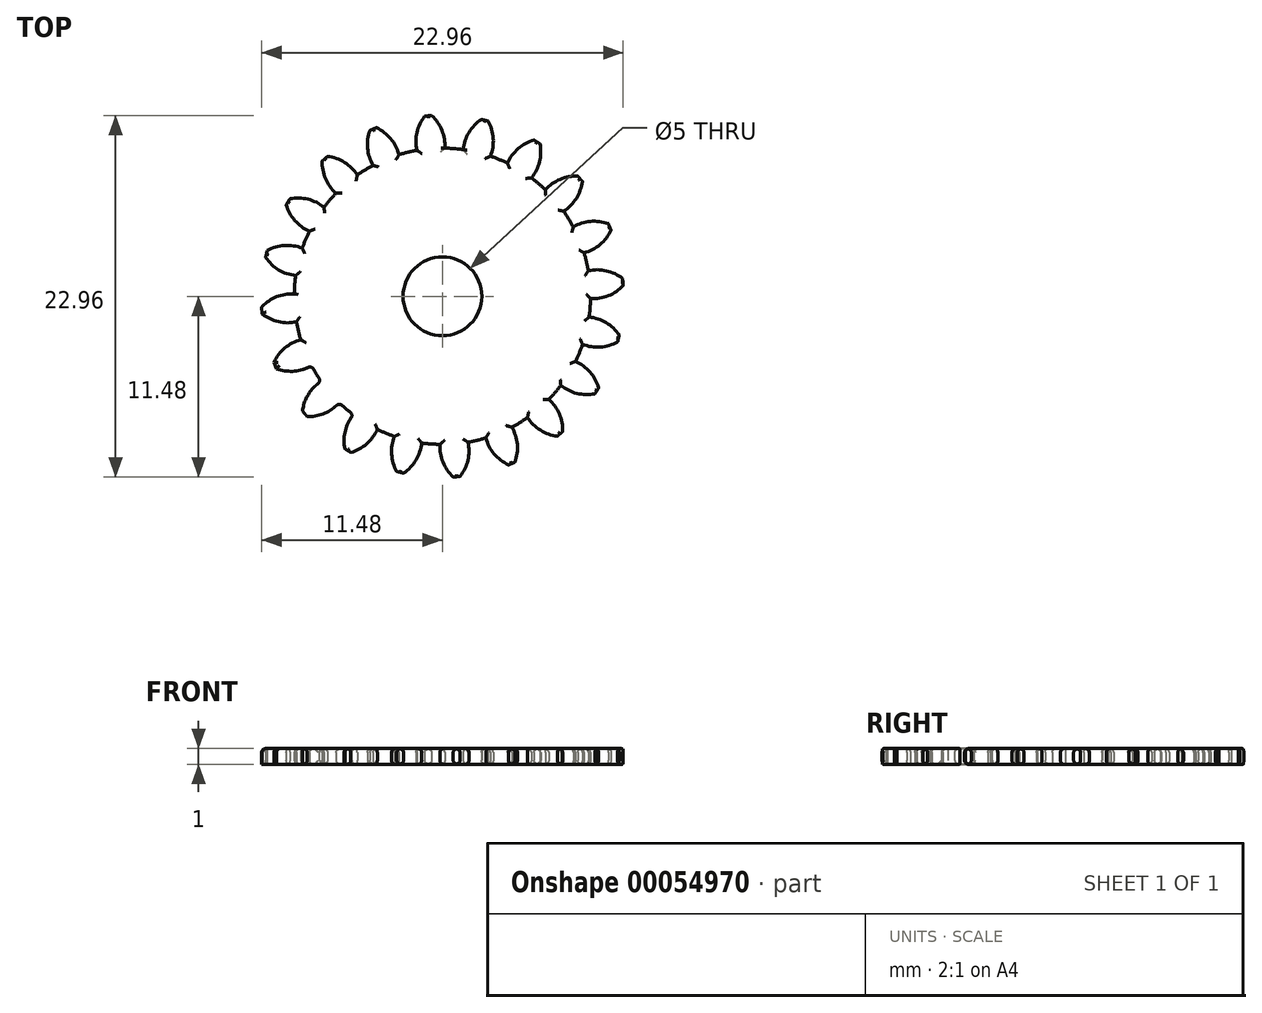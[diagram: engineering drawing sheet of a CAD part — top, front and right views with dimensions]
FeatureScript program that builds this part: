
annotation { "Feature Type Name" : "Feature", "Feature Type Description" : "" }
export const myFeature = defineFeature(function(context is Context, id is Id, definition is map)
    precondition{}
    {
        {
            assignVariable(context, id + "F0", {"name" : "GearDepth", "anyValue" : 1});
        }
        {
            assignVariable(context, id + "F1", {"name" : "TeethFillet", "anyValue" : getVariable(context, 'GearDepth') * .25});
        }
        {
            var Q0;
            Q0=qCreatedBy(makeId("Top.planeOp"),FACE);
            var sketch = newSketch(context, id + "F2", { "sketchPlane" : qUnion([Q0])});
            skCircle(sketch, "E0", {"center": v(0, 0) * mm, "radius": 9.4 * mm});
            skCircle(sketch, "E1", {"center": v(0, 0) * mm, "radius": 10.45 * mm, "construction": true});
            skCircle(sketch, "E2", {"center": v(0, 0) * mm, "radius": 11.5 * mm, "construction": true});
            skLineSegment(sketch, "E3", {"start": v(0, 0) * mm, "end": v(0, 17.6) * mm, "construction": true});
            skLineSegment(sketch, "E4", {"start": v(0, 0) * mm, "end": v(-1.42, 18) * mm, "construction": true});
            skLineSegment(sketch, "E5", {"start": v(0, 10.45) * mm, "end": v(-10.54, 10.45) * mm, "construction": true});
            skLineSegment(sketch, "E6", {"start": v(0, 10.45) * mm, "end": v(-10.3, 6.7) * mm, "construction": true});
            skCircle(sketch, "E7", {"center": v(0, 10.45) * mm, "radius": 2.61 * mm, "construction": true});
            skCircle(sketch, "E8", {"center": v(-2.46, 9.56) * mm, "radius": 2.61 * mm, "construction": true});
            skArc(sketch, "E9", {"start": v(-4.91, 10.45) * mm, "mid": v(-4.92, 10.42) * mm, "end": v(-4.94, 10.39) * mm});
            skArc(sketch, "E10.trimOffspring", {"start": v(0.15, 9.4) * mm, "mid": v(-0.03, 10.54) * mm, "end": v(-0.68, 11.48) * mm});
            skArc(sketch, "E11.MirrorCS", {"start": v(-1.62, 9.27) * mm, "mid": v(-1.62, 10.41) * mm, "end": v(-1.12, 11.45) * mm});
            skLineSegment(sketch, "E12", {"start": v(-1.12, 11.45) * mm, "end": v(-0.68, 11.48) * mm});
            skArc(sketch, "E13.1.0", {"start": v(-2.76, 9) * mm, "mid": v(-3.29, 10.01) * mm, "end": v(-4.2, 10.7) * mm});
            skLineSegment(sketch, "E13.1.1", {"start": v(-4.6, 10.54) * mm, "end": v(-4.2, 10.7) * mm});
            skArc(sketch, "E13.1.2", {"start": v(-4.4, 8.31) * mm, "mid": v(-4.76, 9.4) * mm, "end": v(-4.6, 10.54) * mm});
            skArc(sketch, "E13.2.0", {"start": v(-5.4, 7.7) * mm, "mid": v(-6.22, 8.5) * mm, "end": v(-7.3, 8.89) * mm});
            skLineSegment(sketch, "E13.2.1", {"start": v(-7.64, 8.6) * mm, "end": v(-7.3, 8.89) * mm});
            skArc(sketch, "E13.2.2", {"start": v(-6.76, 6.54) * mm, "mid": v(-7.43, 7.47) * mm, "end": v(-7.64, 8.6) * mm});
            skArc(sketch, "E13.3.0", {"start": v(-7.52, 5.65) * mm, "mid": v(-8.54, 6.17) * mm, "end": v(-9.69, 6.2) * mm});
            skLineSegment(sketch, "E13.3.1", {"start": v(-9.92, 5.82) * mm, "end": v(-9.69, 6.2) * mm});
            skArc(sketch, "E13.3.2", {"start": v(-8.45, 4.13) * mm, "mid": v(-9.37, 4.81) * mm, "end": v(-9.92, 5.82) * mm});
            skArc(sketch, "E13.4.0", {"start": v(-8.9, 3.05) * mm, "mid": v(-10.03, 3.23) * mm, "end": v(-11.13, 2.9) * mm});
            skLineSegment(sketch, "E13.4.1", {"start": v(-11.23, 2.47) * mm, "end": v(-11.13, 2.9) * mm});
            skArc(sketch, "E13.4.2", {"start": v(-9.32, 1.32) * mm, "mid": v(-10.4, 1.68) * mm, "end": v(-11.23, 2.47) * mm});
            skArc(sketch, "E13.5.0", {"start": v(-9.4, 0.15) * mm, "mid": v(-10.54, -0.03) * mm, "end": v(-11.48, -0.68) * mm});
            skLineSegment(sketch, "E13.5.1", {"start": v(-11.45, -1.12) * mm, "end": v(-11.48, -0.68) * mm});
            skArc(sketch, "E13.5.2", {"start": v(-9.27, -1.62) * mm, "mid": v(-10.41, -1.62) * mm, "end": v(-11.45, -1.12) * mm});
            skArc(sketch, "E13.6.0", {"start": v(-9, -2.76) * mm, "mid": v(-10.01, -3.29) * mm, "end": v(-10.7, -4.2) * mm});
            skLineSegment(sketch, "E13.6.1", {"start": v(-10.54, -4.6) * mm, "end": v(-10.7, -4.2) * mm});
            skArc(sketch, "E13.6.2", {"start": v(-8.31, -4.4) * mm, "mid": v(-9.4, -4.76) * mm, "end": v(-10.54, -4.6) * mm});
            skArc(sketch, "E13.7.0", {"start": v(-7.7, -5.4) * mm, "mid": v(-8.5, -6.22) * mm, "end": v(-8.89, -7.3) * mm});
            skLineSegment(sketch, "E13.7.1", {"start": v(-8.6, -7.64) * mm, "end": v(-8.89, -7.3) * mm});
            skArc(sketch, "E13.7.2", {"start": v(-6.54, -6.76) * mm, "mid": v(-7.47, -7.43) * mm, "end": v(-8.6, -7.64) * mm});
            skArc(sketch, "E13.8.0", {"start": v(-5.65, -7.52) * mm, "mid": v(-6.17, -8.54) * mm, "end": v(-6.2, -9.69) * mm});
            skLineSegment(sketch, "E13.8.1", {"start": v(-5.82, -9.92) * mm, "end": v(-6.2, -9.69) * mm});
            skArc(sketch, "E13.8.2", {"start": v(-4.13, -8.45) * mm, "mid": v(-4.81, -9.37) * mm, "end": v(-5.82, -9.92) * mm});
            skArc(sketch, "E13.9.0", {"start": v(-3.05, -8.9) * mm, "mid": v(-3.23, -10.03) * mm, "end": v(-2.9, -11.13) * mm});
            skLineSegment(sketch, "E13.9.1", {"start": v(-2.47, -11.23) * mm, "end": v(-2.9, -11.13) * mm});
            skArc(sketch, "E13.9.2", {"start": v(-1.32, -9.32) * mm, "mid": v(-1.68, -10.4) * mm, "end": v(-2.47, -11.23) * mm});
            skArc(sketch, "E13.10.0", {"start": v(-0.15, -9.4) * mm, "mid": v(0.03, -10.54) * mm, "end": v(0.68, -11.48) * mm});
            skLineSegment(sketch, "E13.10.1", {"start": v(1.12, -11.45) * mm, "end": v(0.68, -11.48) * mm});
            skArc(sketch, "E13.10.2", {"start": v(1.62, -9.27) * mm, "mid": v(1.62, -10.41) * mm, "end": v(1.12, -11.45) * mm});
            skArc(sketch, "E13.11.0", {"start": v(2.76, -9) * mm, "mid": v(3.29, -10.01) * mm, "end": v(4.2, -10.7) * mm});
            skLineSegment(sketch, "E13.11.1", {"start": v(4.6, -10.54) * mm, "end": v(4.2, -10.7) * mm});
            skArc(sketch, "E13.11.2", {"start": v(4.4, -8.31) * mm, "mid": v(4.76, -9.4) * mm, "end": v(4.6, -10.54) * mm});
            skArc(sketch, "E13.12.0", {"start": v(5.4, -7.7) * mm, "mid": v(6.22, -8.5) * mm, "end": v(7.3, -8.89) * mm});
            skLineSegment(sketch, "E13.12.1", {"start": v(7.64, -8.6) * mm, "end": v(7.3, -8.89) * mm});
            skArc(sketch, "E13.12.2", {"start": v(6.76, -6.54) * mm, "mid": v(7.43, -7.47) * mm, "end": v(7.64, -8.6) * mm});
            skArc(sketch, "E13.13.0", {"start": v(7.52, -5.65) * mm, "mid": v(8.54, -6.17) * mm, "end": v(9.69, -6.2) * mm});
            skLineSegment(sketch, "E13.13.1", {"start": v(9.92, -5.82) * mm, "end": v(9.69, -6.2) * mm});
            skArc(sketch, "E13.13.2", {"start": v(8.45, -4.13) * mm, "mid": v(9.37, -4.81) * mm, "end": v(9.92, -5.82) * mm});
            skArc(sketch, "E13.14.0", {"start": v(8.9, -3.05) * mm, "mid": v(10.03, -3.23) * mm, "end": v(11.13, -2.9) * mm});
            skLineSegment(sketch, "E13.14.1", {"start": v(11.23, -2.47) * mm, "end": v(11.13, -2.9) * mm});
            skArc(sketch, "E13.14.2", {"start": v(9.32, -1.32) * mm, "mid": v(10.4, -1.68) * mm, "end": v(11.23, -2.47) * mm});
            skArc(sketch, "E13.15.0", {"start": v(9.4, -0.15) * mm, "mid": v(10.54, 0.03) * mm, "end": v(11.48, 0.68) * mm});
            skLineSegment(sketch, "E13.15.1", {"start": v(11.45, 1.12) * mm, "end": v(11.48, 0.68) * mm});
            skArc(sketch, "E13.15.2", {"start": v(9.27, 1.62) * mm, "mid": v(10.41, 1.62) * mm, "end": v(11.45, 1.12) * mm});
            skArc(sketch, "E13.16.0", {"start": v(9, 2.76) * mm, "mid": v(10.01, 3.29) * mm, "end": v(10.7, 4.2) * mm});
            skLineSegment(sketch, "E13.16.1", {"start": v(10.54, 4.6) * mm, "end": v(10.7, 4.2) * mm});
            skArc(sketch, "E13.16.2", {"start": v(8.31, 4.4) * mm, "mid": v(9.4, 4.76) * mm, "end": v(10.54, 4.6) * mm});
            skArc(sketch, "E13.17.0", {"start": v(7.7, 5.4) * mm, "mid": v(8.5, 6.22) * mm, "end": v(8.89, 7.3) * mm});
            skLineSegment(sketch, "E13.17.1", {"start": v(8.6, 7.64) * mm, "end": v(8.89, 7.3) * mm});
            skArc(sketch, "E13.17.2", {"start": v(6.54, 6.76) * mm, "mid": v(7.47, 7.43) * mm, "end": v(8.6, 7.64) * mm});
            skArc(sketch, "E13.18.0", {"start": v(5.65, 7.52) * mm, "mid": v(6.17, 8.54) * mm, "end": v(6.2, 9.69) * mm});
            skLineSegment(sketch, "E13.18.1", {"start": v(5.82, 9.92) * mm, "end": v(6.2, 9.69) * mm});
            skArc(sketch, "E13.18.2", {"start": v(4.13, 8.45) * mm, "mid": v(4.81, 9.37) * mm, "end": v(5.82, 9.92) * mm});
            skArc(sketch, "E13.19.0", {"start": v(3.05, 8.9) * mm, "mid": v(3.23, 10.03) * mm, "end": v(2.9, 11.13) * mm});
            skLineSegment(sketch, "E13.19.1", {"start": v(2.47, 11.23) * mm, "end": v(2.9, 11.13) * mm});
            skArc(sketch, "E13.19.2", {"start": v(1.32, 9.32) * mm, "mid": v(1.68, 10.4) * mm, "end": v(2.47, 11.23) * mm});
            skCircle(sketch, "E14", {"center": v(0, 0) * mm, "radius": 2.5 * mm});
            skSolve(sketch);
        }
        {
            var Q0;
            {var subQ0=sQuery(id+"F2.wireOp",EDGE,"E10.trimOffspring");Q0=makeQuery(id+"F2.imprint","IMPRINT",FACE,{"disambiguationData":[TD([[makeQuery(id+"F2.imprint","IMPRINT",EDGE,{"derivedFrom":subQ0}),1.0]])]});}
            var Q1;
            {var subQ0=sQuery(id+"F2.wireOp",EDGE,"E0");var subQ1=makeQuery(id+"F2.imprint","INTERSECT",VERTEX,{"derivedFrom":[subQ0,sQuery(id+"F2.wireOp",EDGE,"E10.trimOffspring")]});Q1=makeQuery(id+"F2.imprint","IMPRINT",FACE,{"disambiguationData":[TD([[makeQuery(id+"F2.imprint","IMPRINT",EDGE,{"disambiguationData":[TD([[subQ1,-1.0]])],"derivedFrom":subQ0}),1.0]])]});}
            var Q2;
            {var subQ0=sQuery(id+"F2.wireOp",EDGE,"E13.1.0");Q2=makeQuery(id+"F2.imprint","IMPRINT",FACE,{"disambiguationData":[TD([[makeQuery(id+"F2.imprint","IMPRINT",EDGE,{"derivedFrom":subQ0}),1.0]])]});}
            var Q3;
            {var subQ0=sQuery(id+"F2.wireOp",EDGE,"E13.2.0");Q3=makeQuery(id+"F2.imprint","IMPRINT",FACE,{"disambiguationData":[TD([[makeQuery(id+"F2.imprint","IMPRINT",EDGE,{"derivedFrom":subQ0}),1.0]])]});}
            var Q4;
            {var subQ0=sQuery(id+"F2.wireOp",EDGE,"E13.3.0");Q4=makeQuery(id+"F2.imprint","IMPRINT",FACE,{"disambiguationData":[TD([[makeQuery(id+"F2.imprint","IMPRINT",EDGE,{"derivedFrom":subQ0}),1.0]])]});}
            var Q5;
            {var subQ0=sQuery(id+"F2.wireOp",EDGE,"E13.4.0");Q5=makeQuery(id+"F2.imprint","IMPRINT",FACE,{"disambiguationData":[TD([[makeQuery(id+"F2.imprint","IMPRINT",EDGE,{"derivedFrom":subQ0}),1.0]])]});}
            var Q6;
            {var subQ0=sQuery(id+"F2.wireOp",EDGE,"E13.5.0");Q6=makeQuery(id+"F2.imprint","IMPRINT",FACE,{"disambiguationData":[TD([[makeQuery(id+"F2.imprint","IMPRINT",EDGE,{"derivedFrom":subQ0}),1.0]])]});}
            var Q7;
            {var subQ0=sQuery(id+"F2.wireOp",EDGE,"E13.6.0");Q7=makeQuery(id+"F2.imprint","IMPRINT",FACE,{"disambiguationData":[TD([[makeQuery(id+"F2.imprint","IMPRINT",EDGE,{"derivedFrom":subQ0}),1.0]])]});}
            var Q8;
            {var subQ0=sQuery(id+"F2.wireOp",EDGE,"E13.7.0");Q8=makeQuery(id+"F2.imprint","IMPRINT",FACE,{"disambiguationData":[TD([[makeQuery(id+"F2.imprint","IMPRINT",EDGE,{"derivedFrom":subQ0}),1.0]])]});}
            var Q9;
            {var subQ0=sQuery(id+"F2.wireOp",EDGE,"E13.8.0");Q9=makeQuery(id+"F2.imprint","IMPRINT",FACE,{"disambiguationData":[TD([[makeQuery(id+"F2.imprint","IMPRINT",EDGE,{"derivedFrom":subQ0}),1.0]])]});}
            var Q10;
            {var subQ0=sQuery(id+"F2.wireOp",EDGE,"E13.9.0");Q10=makeQuery(id+"F2.imprint","IMPRINT",FACE,{"disambiguationData":[TD([[makeQuery(id+"F2.imprint","IMPRINT",EDGE,{"derivedFrom":subQ0}),1.0]])]});}
            var Q11;
            {var subQ0=sQuery(id+"F2.wireOp",EDGE,"E13.10.0");Q11=makeQuery(id+"F2.imprint","IMPRINT",FACE,{"disambiguationData":[TD([[makeQuery(id+"F2.imprint","IMPRINT",EDGE,{"derivedFrom":subQ0}),1.0]])]});}
            var Q12;
            {var subQ0=sQuery(id+"F2.wireOp",EDGE,"E13.11.0");Q12=makeQuery(id+"F2.imprint","IMPRINT",FACE,{"disambiguationData":[TD([[makeQuery(id+"F2.imprint","IMPRINT",EDGE,{"derivedFrom":subQ0}),1.0]])]});}
            var Q13;
            {var subQ0=sQuery(id+"F2.wireOp",EDGE,"E13.12.0");Q13=makeQuery(id+"F2.imprint","IMPRINT",FACE,{"disambiguationData":[TD([[makeQuery(id+"F2.imprint","IMPRINT",EDGE,{"derivedFrom":subQ0}),1.0]])]});}
            var Q14;
            {var subQ0=sQuery(id+"F2.wireOp",EDGE,"E13.13.0");Q14=makeQuery(id+"F2.imprint","IMPRINT",FACE,{"disambiguationData":[TD([[makeQuery(id+"F2.imprint","IMPRINT",EDGE,{"derivedFrom":subQ0}),1.0]])]});}
            var Q15;
            {var subQ0=sQuery(id+"F2.wireOp",EDGE,"E13.14.0");Q15=makeQuery(id+"F2.imprint","IMPRINT",FACE,{"disambiguationData":[TD([[makeQuery(id+"F2.imprint","IMPRINT",EDGE,{"derivedFrom":subQ0}),1.0]])]});}
            var Q16;
            {var subQ0=sQuery(id+"F2.wireOp",EDGE,"E13.15.0");Q16=makeQuery(id+"F2.imprint","IMPRINT",FACE,{"disambiguationData":[TD([[makeQuery(id+"F2.imprint","IMPRINT",EDGE,{"derivedFrom":subQ0}),1.0]])]});}
            var Q17;
            {var subQ0=sQuery(id+"F2.wireOp",EDGE,"E13.16.0");Q17=makeQuery(id+"F2.imprint","IMPRINT",FACE,{"disambiguationData":[TD([[makeQuery(id+"F2.imprint","IMPRINT",EDGE,{"derivedFrom":subQ0}),1.0]])]});}
            var Q18;
            {var subQ0=sQuery(id+"F2.wireOp",EDGE,"E13.17.0");Q18=makeQuery(id+"F2.imprint","IMPRINT",FACE,{"disambiguationData":[TD([[makeQuery(id+"F2.imprint","IMPRINT",EDGE,{"derivedFrom":subQ0}),1.0]])]});}
            var Q19;
            {var subQ0=sQuery(id+"F2.wireOp",EDGE,"E13.18.0");Q19=makeQuery(id+"F2.imprint","IMPRINT",FACE,{"disambiguationData":[TD([[makeQuery(id+"F2.imprint","IMPRINT",EDGE,{"derivedFrom":subQ0}),1.0]])]});}
            var Q20;
            {var subQ0=sQuery(id+"F2.wireOp",EDGE,"E13.19.0");Q20=makeQuery(id+"F2.imprint","IMPRINT",FACE,{"disambiguationData":[TD([[makeQuery(id+"F2.imprint","IMPRINT",EDGE,{"derivedFrom":subQ0}),1.0]])]});}
            var Q21;
            Q21=sQuery(id+"F2.wireOp",EDGE,"E0");
            var Q22;
            Q22=sQuery(id+"F2.wireOp",EDGE,"E10.trimOffspring");
            var Q23;
            Q23=sQuery(id+"F2.wireOp",EDGE,"E12");
            var Q24;
            Q24=sQuery(id+"F2.wireOp",EDGE,"E11.MirrorCS");
            extrude(context, id + "F3", {"entities" : qUnion([Q0, Q1, Q2, Q3, Q4, Q5, Q6, Q7, Q8, Q9, Q10, Q11, Q12, Q13, Q14, Q15, Q16, Q17, Q18, Q19, Q20]), "surfaceEntities" : qUnion([Q21, Q22, Q23, Q24]), "depth" : (getVariable(context, 'GearDepth')) * mm});
        }
        {
            var Q0;
            Q0=makeQuery(id+"F3.opExtrude","CAP_EDGE",EDGE,{"disambiguationData":[OSD([sQuery(id+"F2.wireOp",EDGE,"E13.5.2")])],"isStart":false});
            var Q1;
            Q1=makeQuery(id+"F3.opExtrude","CAP_EDGE",EDGE,{"disambiguationData":[OSD([sQuery(id+"F2.wireOp",EDGE,"E13.5.1")])],"isStart":false});
            var Q2;
            {var subQ0=sQuery(id+"F2.wireOp",EDGE,"E0");Q2=makeQuery(id+"F3.opExtrude","CAP_EDGE",EDGE,{"disambiguationData":[OSD([subQ0]),TDD([makeQuery(id+"F2.imprint","IMPRINT",EDGE,{"disambiguationData":[TD([[makeQuery(id+"F2.imprint","INTERSECT",VERTEX,{"derivedFrom":[subQ0,sQuery(id+"F2.wireOp",EDGE,"E13.5.2")]}),-1.0]])],"derivedFrom":subQ0})])],"isStart":false});}
            var Q3;
            Q3=makeQuery(id+"F3.opExtrude","CAP_EDGE",EDGE,{"disambiguationData":[OSD([sQuery(id+"F2.wireOp",EDGE,"E13.6.0")])],"isStart":false});
            var Q4;
            Q4=makeQuery(id+"F3.opExtrude","CAP_EDGE",EDGE,{"disambiguationData":[OSD([sQuery(id+"F2.wireOp",EDGE,"E13.6.1")])],"isStart":false});
            var Q5;
            Q5=makeQuery(id+"F3.opExtrude","CAP_EDGE",EDGE,{"disambiguationData":[OSD([sQuery(id+"F2.wireOp",EDGE,"E13.6.2")])],"isStart":false});
            var Q6;
            {var subQ0=sQuery(id+"F2.wireOp",EDGE,"E0");Q6=makeQuery(id+"F3.opExtrude","SWEPT_FACE",FACE,{"disambiguationData":[OSD([subQ0]),TDD([makeQuery(id+"F2.imprint","IMPRINT",EDGE,{"disambiguationData":[TD([[makeQuery(id+"F2.imprint","INTERSECT",VERTEX,{"derivedFrom":[subQ0,sQuery(id+"F2.wireOp",EDGE,"E13.6.2")]}),-1.0]])],"derivedFrom":subQ0})])]});}
            var Q7;
            {var subQ0=sQuery(id+"F2.wireOp",EDGE,"E0");Q7=makeQuery(id+"F3.opExtrude","CAP_EDGE",EDGE,{"disambiguationData":[OSD([subQ0]),TDD([makeQuery(id+"F2.imprint","IMPRINT",EDGE,{"disambiguationData":[TD([[makeQuery(id+"F2.imprint","INTERSECT",VERTEX,{"derivedFrom":[subQ0,sQuery(id+"F2.wireOp",EDGE,"E13.6.2")]}),-1.0]])],"derivedFrom":subQ0})])],"isStart":false});}
            var Q8;
            Q8=makeQuery(id+"F3.opExtrude","CAP_EDGE",EDGE,{"disambiguationData":[OSD([sQuery(id+"F2.wireOp",EDGE,"E13.7.2")])],"isStart":true});
            var Q9;
            {var subQ0=sQuery(id+"F2.wireOp",EDGE,"E0");Q9=makeQuery(id+"F3.opExtrude","CAP_EDGE",EDGE,{"disambiguationData":[OSD([subQ0]),TDD([makeQuery(id+"F2.imprint","IMPRINT",EDGE,{"disambiguationData":[TD([[makeQuery(id+"F2.imprint","INTERSECT",VERTEX,{"derivedFrom":[subQ0,sQuery(id+"F2.wireOp",EDGE,"E13.7.2")]}),-1.0]])],"derivedFrom":subQ0})])],"isStart":true});}
            var Q10;
            Q10=makeQuery(id+"F3.opExtrude","CAP_EDGE",EDGE,{"disambiguationData":[OSD([sQuery(id+"F2.wireOp",EDGE,"E13.7.2")])],"isStart":false});
            var Q11;
            {var subQ0=sQuery(id+"F2.wireOp",EDGE,"E0");Q11=makeQuery(id+"F3.opExtrude","CAP_EDGE",EDGE,{"disambiguationData":[OSD([subQ0]),TDD([makeQuery(id+"F2.imprint","IMPRINT",EDGE,{"disambiguationData":[TD([[makeQuery(id+"F2.imprint","INTERSECT",VERTEX,{"derivedFrom":[subQ0,sQuery(id+"F2.wireOp",EDGE,"E13.7.2")]}),-1.0]])],"derivedFrom":subQ0})])],"isStart":false});}
            var Q12;
            Q12=makeQuery(id+"F3.opExtrude","CAP_EDGE",EDGE,{"disambiguationData":[OSD([sQuery(id+"F2.wireOp",EDGE,"E13.8.0")])],"isStart":false});
            var Q13;
            {var subQ0=sQuery(id+"F2.wireOp",EDGE,"E0");Q13=makeQuery(id+"F3.opExtrude","SWEPT_FACE",FACE,{"disambiguationData":[OSD([subQ0]),TDD([makeQuery(id+"F2.imprint","IMPRINT",EDGE,{"disambiguationData":[TD([[makeQuery(id+"F2.imprint","INTERSECT",VERTEX,{"derivedFrom":[subQ0,sQuery(id+"F2.wireOp",EDGE,"E13.7.2")]}),-1.0]])],"derivedFrom":subQ0})])]});}
            var Q14;
            Q14=makeQuery(id+"F3.opExtrude","CAP_EDGE",EDGE,{"disambiguationData":[OSD([sQuery(id+"F2.wireOp",EDGE,"E13.6.0")])],"isStart":true});
            var Q15;
            Q15=makeQuery(id+"F3.opExtrude","CAP_EDGE",EDGE,{"disambiguationData":[OSD([sQuery(id+"F2.wireOp",EDGE,"E13.8.2")])],"isStart":false});
            var Q16;
            {var subQ0=sQuery(id+"F2.wireOp",EDGE,"E0");Q16=makeQuery(id+"F3.opExtrude","CAP_EDGE",EDGE,{"disambiguationData":[OSD([subQ0]),TDD([makeQuery(id+"F2.imprint","IMPRINT",EDGE,{"disambiguationData":[TD([[makeQuery(id+"F2.imprint","INTERSECT",VERTEX,{"derivedFrom":[subQ0,sQuery(id+"F2.wireOp",EDGE,"E13.8.2")]}),-1.0]])],"derivedFrom":subQ0})])],"isStart":false});}
            var Q17;
            Q17=makeQuery(id+"F3.opExtrude","CAP_EDGE",EDGE,{"disambiguationData":[OSD([sQuery(id+"F2.wireOp",EDGE,"E13.9.0")])],"isStart":false});
            var Q18;
            Q18=makeQuery(id+"F3.opExtrude","CAP_EDGE",EDGE,{"disambiguationData":[OSD([sQuery(id+"F2.wireOp",EDGE,"E13.9.2")])],"isStart":false});
            var Q19;
            {var subQ0=sQuery(id+"F2.wireOp",EDGE,"E0");Q19=makeQuery(id+"F3.opExtrude","CAP_EDGE",EDGE,{"disambiguationData":[OSD([subQ0]),TDD([makeQuery(id+"F2.imprint","IMPRINT",EDGE,{"disambiguationData":[TD([[makeQuery(id+"F2.imprint","INTERSECT",VERTEX,{"derivedFrom":[subQ0,sQuery(id+"F2.wireOp",EDGE,"E13.9.2")]}),-1.0]])],"derivedFrom":subQ0})])],"isStart":false});}
            var Q20;
            Q20=makeQuery(id+"F3.opExtrude","CAP_EDGE",EDGE,{"disambiguationData":[OSD([sQuery(id+"F2.wireOp",EDGE,"E13.10.0")])],"isStart":false});
            var Q21;
            Q21=makeQuery(id+"F3.opExtrude","CAP_EDGE",EDGE,{"disambiguationData":[OSD([sQuery(id+"F2.wireOp",EDGE,"E13.10.2")])],"isStart":false});
            var Q22;
            {var subQ0=sQuery(id+"F2.wireOp",EDGE,"E0");Q22=makeQuery(id+"F3.opExtrude","CAP_EDGE",EDGE,{"disambiguationData":[OSD([subQ0]),TDD([makeQuery(id+"F2.imprint","IMPRINT",EDGE,{"disambiguationData":[TD([[makeQuery(id+"F2.imprint","INTERSECT",VERTEX,{"derivedFrom":[subQ0,sQuery(id+"F2.wireOp",EDGE,"E13.10.2")]}),-1.0]])],"derivedFrom":subQ0})])],"isStart":false});}
            var Q23;
            Q23=makeQuery(id+"F3.opExtrude","CAP_EDGE",EDGE,{"disambiguationData":[OSD([sQuery(id+"F2.wireOp",EDGE,"E13.11.0")])],"isStart":false});
            var Q24;
            Q24=makeQuery(id+"F3.opExtrude","CAP_EDGE",EDGE,{"disambiguationData":[OSD([sQuery(id+"F2.wireOp",EDGE,"E13.11.2")])],"isStart":false});
            var Q25;
            {var subQ0=sQuery(id+"F2.wireOp",EDGE,"E0");Q25=makeQuery(id+"F3.opExtrude","CAP_EDGE",EDGE,{"disambiguationData":[OSD([subQ0]),TDD([makeQuery(id+"F2.imprint","IMPRINT",EDGE,{"disambiguationData":[TD([[makeQuery(id+"F2.imprint","INTERSECT",VERTEX,{"derivedFrom":[subQ0,sQuery(id+"F2.wireOp",EDGE,"E13.11.2")]}),-1.0]])],"derivedFrom":subQ0})])],"isStart":false});}
            var Q26;
            Q26=makeQuery(id+"F3.opExtrude","CAP_EDGE",EDGE,{"disambiguationData":[OSD([sQuery(id+"F2.wireOp",EDGE,"E13.12.0")])],"isStart":false});
            var Q27;
            Q27=makeQuery(id+"F3.opExtrude","CAP_EDGE",EDGE,{"disambiguationData":[OSD([sQuery(id+"F2.wireOp",EDGE,"E13.12.2")])],"isStart":false});
            var Q28;
            {var subQ0=sQuery(id+"F2.wireOp",EDGE,"E0");Q28=makeQuery(id+"F3.opExtrude","CAP_EDGE",EDGE,{"disambiguationData":[OSD([subQ0]),TDD([makeQuery(id+"F2.imprint","IMPRINT",EDGE,{"disambiguationData":[TD([[makeQuery(id+"F2.imprint","INTERSECT",VERTEX,{"derivedFrom":[subQ0,sQuery(id+"F2.wireOp",EDGE,"E13.12.2")]}),-1.0]])],"derivedFrom":subQ0})])],"isStart":false});}
            var Q29;
            Q29=makeQuery(id+"F3.opExtrude","CAP_EDGE",EDGE,{"disambiguationData":[OSD([sQuery(id+"F2.wireOp",EDGE,"E13.13.0")])],"isStart":false});
            var Q30;
            Q30=makeQuery(id+"F3.opExtrude","CAP_EDGE",EDGE,{"disambiguationData":[OSD([sQuery(id+"F2.wireOp",EDGE,"E13.13.2")])],"isStart":false});
            var Q31;
            {var subQ0=sQuery(id+"F2.wireOp",EDGE,"E0");Q31=makeQuery(id+"F3.opExtrude","CAP_EDGE",EDGE,{"disambiguationData":[OSD([subQ0]),TDD([makeQuery(id+"F2.imprint","IMPRINT",EDGE,{"disambiguationData":[TD([[makeQuery(id+"F2.imprint","INTERSECT",VERTEX,{"derivedFrom":[subQ0,sQuery(id+"F2.wireOp",EDGE,"E13.13.2")]}),-1.0]])],"derivedFrom":subQ0})])],"isStart":false});}
            var Q32;
            Q32=makeQuery(id+"F3.opExtrude","CAP_EDGE",EDGE,{"disambiguationData":[OSD([sQuery(id+"F2.wireOp",EDGE,"E13.14.0")])],"isStart":false});
            var Q33;
            Q33=makeQuery(id+"F3.opExtrude","CAP_EDGE",EDGE,{"disambiguationData":[OSD([sQuery(id+"F2.wireOp",EDGE,"E13.14.2")])],"isStart":false});
            var Q34;
            {var subQ0=sQuery(id+"F2.wireOp",EDGE,"E0");Q34=makeQuery(id+"F3.opExtrude","CAP_EDGE",EDGE,{"disambiguationData":[OSD([subQ0]),TDD([makeQuery(id+"F2.imprint","IMPRINT",EDGE,{"disambiguationData":[TD([[makeQuery(id+"F2.imprint","INTERSECT",VERTEX,{"derivedFrom":[subQ0,sQuery(id+"F2.wireOp",EDGE,"E13.14.2")]}),-1.0]])],"derivedFrom":subQ0})])],"isStart":false});}
            var Q35;
            Q35=makeQuery(id+"F3.opExtrude","CAP_EDGE",EDGE,{"disambiguationData":[OSD([sQuery(id+"F2.wireOp",EDGE,"E13.15.0")])],"isStart":false});
            var Q36;
            {var subQ0=sQuery(id+"F2.wireOp",EDGE,"E0");Q36=makeQuery(id+"F3.opExtrude","CAP_EDGE",EDGE,{"disambiguationData":[OSD([subQ0]),TDD([makeQuery(id+"F2.imprint","IMPRINT",EDGE,{"disambiguationData":[TD([[makeQuery(id+"F2.imprint","INTERSECT",VERTEX,{"derivedFrom":[subQ0,sQuery(id+"F2.wireOp",EDGE,"E13.14.2")]}),-1.0]])],"derivedFrom":subQ0})])],"isStart":false});}
            var Q37;
            Q37=makeQuery(id+"F3.opExtrude","CAP_EDGE",EDGE,{"disambiguationData":[OSD([sQuery(id+"F2.wireOp",EDGE,"E13.15.2")])],"isStart":false});
            var Q38;
            {var subQ0=sQuery(id+"F2.wireOp",EDGE,"E0");Q38=makeQuery(id+"F3.opExtrude","CAP_EDGE",EDGE,{"disambiguationData":[OSD([subQ0]),TDD([makeQuery(id+"F2.imprint","IMPRINT",EDGE,{"disambiguationData":[TD([[makeQuery(id+"F2.imprint","INTERSECT",VERTEX,{"derivedFrom":[subQ0,sQuery(id+"F2.wireOp",EDGE,"E13.15.2")]}),-1.0]])],"derivedFrom":subQ0})])],"isStart":false});}
            var Q39;
            Q39=makeQuery(id+"F3.opExtrude","CAP_EDGE",EDGE,{"disambiguationData":[OSD([sQuery(id+"F2.wireOp",EDGE,"E13.16.0")])],"isStart":false});
            var Q40;
            Q40=makeQuery(id+"F3.opExtrude","CAP_EDGE",EDGE,{"disambiguationData":[OSD([sQuery(id+"F2.wireOp",EDGE,"E13.16.2")])],"isStart":false});
            var Q41;
            Q41=makeQuery(id+"F3.opExtrude","CAP_EDGE",EDGE,{"disambiguationData":[OSD([sQuery(id+"F2.wireOp",EDGE,"E13.17.0")])],"isStart":false});
            var Q42;
            {var subQ0=sQuery(id+"F2.wireOp",EDGE,"E0");Q42=makeQuery(id+"F3.opExtrude","CAP_EDGE",EDGE,{"disambiguationData":[OSD([subQ0]),TDD([makeQuery(id+"F2.imprint","IMPRINT",EDGE,{"disambiguationData":[TD([[makeQuery(id+"F2.imprint","INTERSECT",VERTEX,{"derivedFrom":[subQ0,sQuery(id+"F2.wireOp",EDGE,"E13.16.2")]}),-1.0]])],"derivedFrom":subQ0})])],"isStart":false});}
            var Q43;
            Q43=makeQuery(id+"F3.opExtrude","CAP_EDGE",EDGE,{"disambiguationData":[OSD([sQuery(id+"F2.wireOp",EDGE,"E13.17.2")])],"isStart":false});
            var Q44;
            {var subQ0=sQuery(id+"F2.wireOp",EDGE,"E0");Q44=makeQuery(id+"F3.opExtrude","CAP_EDGE",EDGE,{"disambiguationData":[OSD([subQ0]),TDD([makeQuery(id+"F2.imprint","IMPRINT",EDGE,{"disambiguationData":[TD([[makeQuery(id+"F2.imprint","INTERSECT",VERTEX,{"derivedFrom":[subQ0,sQuery(id+"F2.wireOp",EDGE,"E13.17.2")]}),-1.0]])],"derivedFrom":subQ0})])],"isStart":false});}
            var Q45;
            Q45=makeQuery(id+"F3.opExtrude","CAP_EDGE",EDGE,{"disambiguationData":[OSD([sQuery(id+"F2.wireOp",EDGE,"E13.18.0")])],"isStart":false});
            var Q46;
            Q46=makeQuery(id+"F3.opExtrude","CAP_EDGE",EDGE,{"disambiguationData":[OSD([sQuery(id+"F2.wireOp",EDGE,"E13.18.2")])],"isStart":false});
            var Q47;
            {var subQ0=sQuery(id+"F2.wireOp",EDGE,"E0");Q47=makeQuery(id+"F3.opExtrude","CAP_EDGE",EDGE,{"disambiguationData":[OSD([subQ0]),TDD([makeQuery(id+"F2.imprint","IMPRINT",EDGE,{"disambiguationData":[TD([[makeQuery(id+"F2.imprint","INTERSECT",VERTEX,{"derivedFrom":[subQ0,sQuery(id+"F2.wireOp",EDGE,"E13.18.2")]}),-1.0]])],"derivedFrom":subQ0})])],"isStart":false});}
            var Q48;
            Q48=makeQuery(id+"F3.opExtrude","CAP_EDGE",EDGE,{"disambiguationData":[OSD([sQuery(id+"F2.wireOp",EDGE,"E13.19.0")])],"isStart":false});
            var Q49;
            Q49=makeQuery(id+"F3.opExtrude","CAP_EDGE",EDGE,{"disambiguationData":[OSD([sQuery(id+"F2.wireOp",EDGE,"E13.19.2")])],"isStart":false});
            var Q50;
            Q50=makeQuery(id+"F3.opExtrude","CAP_EDGE",EDGE,{"disambiguationData":[OSD([sQuery(id+"F2.wireOp",EDGE,"E10.trimOffspring")])],"isStart":false});
            var Q51;
            Q51=makeQuery(id+"F3.opExtrude","CAP_EDGE",EDGE,{"disambiguationData":[OSD([sQuery(id+"F2.wireOp",EDGE,"E11.MirrorCS")])],"isStart":false});
            var Q52;
            {var subQ0=sQuery(id+"F2.wireOp",EDGE,"E0");Q52=makeQuery(id+"F3.opExtrude","CAP_EDGE",EDGE,{"disambiguationData":[OSD([subQ0]),TDD([makeQuery(id+"F2.imprint","IMPRINT",EDGE,{"disambiguationData":[TD([[makeQuery(id+"F2.imprint","INTERSECT",VERTEX,{"derivedFrom":[subQ0,sQuery(id+"F2.wireOp",EDGE,"E11.MirrorCS")]}),-1.0]])],"derivedFrom":subQ0})])],"isStart":false});}
            var Q53;
            Q53=makeQuery(id+"F3.opExtrude","CAP_EDGE",EDGE,{"disambiguationData":[OSD([sQuery(id+"F2.wireOp",EDGE,"E13.1.0")])],"isStart":false});
            var Q54;
            Q54=makeQuery(id+"F3.opExtrude","CAP_EDGE",EDGE,{"disambiguationData":[OSD([sQuery(id+"F2.wireOp",EDGE,"E13.1.2")])],"isStart":false});
            var Q55;
            {var subQ0=sQuery(id+"F2.wireOp",EDGE,"E0");Q55=makeQuery(id+"F3.opExtrude","CAP_EDGE",EDGE,{"disambiguationData":[OSD([subQ0]),TDD([makeQuery(id+"F2.imprint","IMPRINT",EDGE,{"disambiguationData":[TD([[makeQuery(id+"F2.imprint","INTERSECT",VERTEX,{"derivedFrom":[subQ0,sQuery(id+"F2.wireOp",EDGE,"E13.1.2")]}),-1.0]])],"derivedFrom":subQ0})])],"isStart":false});}
            var Q56;
            Q56=makeQuery(id+"F3.opExtrude","CAP_EDGE",EDGE,{"disambiguationData":[OSD([sQuery(id+"F2.wireOp",EDGE,"E13.2.0")])],"isStart":false});
            var Q57;
            Q57=makeQuery(id+"F3.opExtrude","CAP_EDGE",EDGE,{"disambiguationData":[OSD([sQuery(id+"F2.wireOp",EDGE,"E13.2.2")])],"isStart":false});
            var Q58;
            {var subQ0=sQuery(id+"F2.wireOp",EDGE,"E0");Q58=makeQuery(id+"F3.opExtrude","CAP_EDGE",EDGE,{"disambiguationData":[OSD([subQ0]),TDD([makeQuery(id+"F2.imprint","IMPRINT",EDGE,{"disambiguationData":[TD([[makeQuery(id+"F2.imprint","INTERSECT",VERTEX,{"derivedFrom":[subQ0,sQuery(id+"F2.wireOp",EDGE,"E13.2.2")]}),-1.0]])],"derivedFrom":subQ0})])],"isStart":false});}
            var Q59;
            Q59=makeQuery(id+"F3.opExtrude","CAP_EDGE",EDGE,{"disambiguationData":[OSD([sQuery(id+"F2.wireOp",EDGE,"E13.3.0")])],"isStart":false});
            var Q60;
            Q60=makeQuery(id+"F3.opExtrude","CAP_EDGE",EDGE,{"disambiguationData":[OSD([sQuery(id+"F2.wireOp",EDGE,"E13.3.2")])],"isStart":false});
            var Q61;
            {var subQ0=sQuery(id+"F2.wireOp",EDGE,"E0");Q61=makeQuery(id+"F3.opExtrude","CAP_EDGE",EDGE,{"disambiguationData":[OSD([subQ0]),TDD([makeQuery(id+"F2.imprint","IMPRINT",EDGE,{"disambiguationData":[TD([[makeQuery(id+"F2.imprint","INTERSECT",VERTEX,{"derivedFrom":[subQ0,sQuery(id+"F2.wireOp",EDGE,"E13.3.2")]}),-1.0]])],"derivedFrom":subQ0})])],"isStart":false});}
            var Q62;
            Q62=makeQuery(id+"F3.opExtrude","CAP_EDGE",EDGE,{"disambiguationData":[OSD([sQuery(id+"F2.wireOp",EDGE,"E13.4.0")])],"isStart":false});
            var Q63;
            Q63=makeQuery(id+"F3.opExtrude","CAP_EDGE",EDGE,{"disambiguationData":[OSD([sQuery(id+"F2.wireOp",EDGE,"E13.4.2")])],"isStart":false});
            var Q64;
            {var subQ0=sQuery(id+"F2.wireOp",EDGE,"E0");Q64=makeQuery(id+"F3.opExtrude","CAP_EDGE",EDGE,{"disambiguationData":[OSD([subQ0]),TDD([makeQuery(id+"F2.imprint","IMPRINT",EDGE,{"disambiguationData":[TD([[makeQuery(id+"F2.imprint","INTERSECT",VERTEX,{"derivedFrom":[subQ0,sQuery(id+"F2.wireOp",EDGE,"E13.4.2")]}),-1.0]])],"derivedFrom":subQ0})])],"isStart":false});}
            var Q65;
            {var subQ0=sQuery(id+"F2.wireOp",EDGE,"E0");Q65=makeQuery(id+"F3.opExtrude","CAP_EDGE",EDGE,{"disambiguationData":[OSD([subQ0]),TDD([makeQuery(id+"F2.imprint","IMPRINT",EDGE,{"disambiguationData":[TD([[makeQuery(id+"F2.imprint","INTERSECT",VERTEX,{"derivedFrom":[subQ0,sQuery(id+"F2.wireOp",EDGE,"E13.5.2")]}),-1.0]])],"derivedFrom":subQ0})])],"isStart":true});}
            var Q66;
            Q66=makeQuery(id+"F3.opExtrude","CAP_EDGE",EDGE,{"disambiguationData":[OSD([sQuery(id+"F2.wireOp",EDGE,"E13.5.2")])],"isStart":true});
            var Q67;
            {var subQ0=sQuery(id+"F2.wireOp",EDGE,"E0");Q67=makeQuery(id+"F3.opExtrude","CAP_EDGE",EDGE,{"disambiguationData":[OSD([subQ0]),TDD([makeQuery(id+"F2.imprint","IMPRINT",EDGE,{"disambiguationData":[TD([[makeQuery(id+"F2.imprint","INTERSECT",VERTEX,{"derivedFrom":[subQ0,sQuery(id+"F2.wireOp",EDGE,"E13.4.2")]}),-1.0]])],"derivedFrom":subQ0})])],"isStart":true});}
            var Q68;
            Q68=makeQuery(id+"F3.opExtrude","CAP_EDGE",EDGE,{"disambiguationData":[OSD([sQuery(id+"F2.wireOp",EDGE,"E13.4.2")])],"isStart":true});
            var Q69;
            Q69=makeQuery(id+"F3.opExtrude","CAP_EDGE",EDGE,{"disambiguationData":[OSD([sQuery(id+"F2.wireOp",EDGE,"E13.4.0")])],"isStart":true});
            var Q70;
            {var subQ0=sQuery(id+"F2.wireOp",EDGE,"E0");Q70=makeQuery(id+"F3.opExtrude","CAP_EDGE",EDGE,{"disambiguationData":[OSD([subQ0]),TDD([makeQuery(id+"F2.imprint","IMPRINT",EDGE,{"disambiguationData":[TD([[makeQuery(id+"F2.imprint","INTERSECT",VERTEX,{"derivedFrom":[subQ0,sQuery(id+"F2.wireOp",EDGE,"E13.3.2")]}),-1.0]])],"derivedFrom":subQ0})])],"isStart":true});}
            var Q71;
            Q71=makeQuery(id+"F3.opExtrude","CAP_EDGE",EDGE,{"disambiguationData":[OSD([sQuery(id+"F2.wireOp",EDGE,"E13.3.2")])],"isStart":true});
            var Q72;
            Q72=makeQuery(id+"F3.opExtrude","CAP_EDGE",EDGE,{"disambiguationData":[OSD([sQuery(id+"F2.wireOp",EDGE,"E13.3.0")])],"isStart":true});
            var Q73;
            {var subQ0=sQuery(id+"F2.wireOp",EDGE,"E0");Q73=makeQuery(id+"F3.opExtrude","CAP_EDGE",EDGE,{"disambiguationData":[OSD([subQ0]),TDD([makeQuery(id+"F2.imprint","IMPRINT",EDGE,{"disambiguationData":[TD([[makeQuery(id+"F2.imprint","INTERSECT",VERTEX,{"derivedFrom":[subQ0,sQuery(id+"F2.wireOp",EDGE,"E13.2.2")]}),-1.0]])],"derivedFrom":subQ0})])],"isStart":true});}
            var Q74;
            Q74=makeQuery(id+"F3.opExtrude","CAP_EDGE",EDGE,{"disambiguationData":[OSD([sQuery(id+"F2.wireOp",EDGE,"E13.2.2")])],"isStart":true});
            var Q75;
            Q75=makeQuery(id+"F3.opExtrude","CAP_EDGE",EDGE,{"disambiguationData":[OSD([sQuery(id+"F2.wireOp",EDGE,"E13.2.0")])],"isStart":true});
            var Q76;
            Q76=makeQuery(id+"F3.opExtrude","CAP_EDGE",EDGE,{"disambiguationData":[OSD([sQuery(id+"F2.wireOp",EDGE,"E13.1.2")])],"isStart":true});
            var Q77;
            {var subQ0=sQuery(id+"F2.wireOp",EDGE,"E0");Q77=makeQuery(id+"F3.opExtrude","CAP_EDGE",EDGE,{"disambiguationData":[OSD([subQ0]),TDD([makeQuery(id+"F2.imprint","IMPRINT",EDGE,{"disambiguationData":[TD([[makeQuery(id+"F2.imprint","INTERSECT",VERTEX,{"derivedFrom":[subQ0,sQuery(id+"F2.wireOp",EDGE,"E13.1.2")]}),-1.0]])],"derivedFrom":subQ0})])],"isStart":true});}
            var Q78;
            Q78=makeQuery(id+"F3.opExtrude","CAP_EDGE",EDGE,{"disambiguationData":[OSD([sQuery(id+"F2.wireOp",EDGE,"E13.1.0")])],"isStart":true});
            var Q79;
            {var subQ0=sQuery(id+"F2.wireOp",EDGE,"E0");Q79=makeQuery(id+"F3.opExtrude","CAP_EDGE",EDGE,{"disambiguationData":[OSD([subQ0]),TDD([makeQuery(id+"F2.imprint","IMPRINT",EDGE,{"disambiguationData":[TD([[makeQuery(id+"F2.imprint","INTERSECT",VERTEX,{"derivedFrom":[subQ0,sQuery(id+"F2.wireOp",EDGE,"E11.MirrorCS")]}),-1.0]])],"derivedFrom":subQ0})])],"isStart":true});}
            var Q80;
            Q80=makeQuery(id+"F3.opExtrude","CAP_EDGE",EDGE,{"disambiguationData":[OSD([sQuery(id+"F2.wireOp",EDGE,"E11.MirrorCS")])],"isStart":true});
            var Q81;
            Q81=makeQuery(id+"F3.opExtrude","CAP_EDGE",EDGE,{"disambiguationData":[OSD([sQuery(id+"F2.wireOp",EDGE,"E10.trimOffspring")])],"isStart":true});
            var Q82;
            {var subQ0=sQuery(id+"F2.wireOp",EDGE,"E0");Q82=makeQuery(id+"F3.opExtrude","CAP_EDGE",EDGE,{"disambiguationData":[OSD([subQ0]),TDD([makeQuery(id+"F2.imprint","IMPRINT",EDGE,{"disambiguationData":[TD([[makeQuery(id+"F2.imprint","INTERSECT",VERTEX,{"derivedFrom":[subQ0,sQuery(id+"F2.wireOp",EDGE,"E10.trimOffspring")]}),1.0]])],"derivedFrom":subQ0})])],"isStart":true});}
            var Q83;
            Q83=makeQuery(id+"F3.opExtrude","CAP_EDGE",EDGE,{"disambiguationData":[OSD([sQuery(id+"F2.wireOp",EDGE,"E13.19.2")])],"isStart":true});
            var Q84;
            Q84=makeQuery(id+"F3.opExtrude","CAP_EDGE",EDGE,{"disambiguationData":[OSD([sQuery(id+"F2.wireOp",EDGE,"E13.19.0")])],"isStart":true});
            var Q85;
            {var subQ0=sQuery(id+"F2.wireOp",EDGE,"E0");Q85=makeQuery(id+"F3.opExtrude","CAP_EDGE",EDGE,{"disambiguationData":[OSD([subQ0]),TDD([makeQuery(id+"F2.imprint","IMPRINT",EDGE,{"disambiguationData":[TD([[makeQuery(id+"F2.imprint","INTERSECT",VERTEX,{"derivedFrom":[subQ0,sQuery(id+"F2.wireOp",EDGE,"E13.18.2")]}),-1.0]])],"derivedFrom":subQ0})])],"isStart":true});}
            var Q86;
            Q86=makeQuery(id+"F3.opExtrude","CAP_EDGE",EDGE,{"disambiguationData":[OSD([sQuery(id+"F2.wireOp",EDGE,"E13.18.2")])],"isStart":true});
            var Q87;
            Q87=makeQuery(id+"F3.opExtrude","CAP_EDGE",EDGE,{"disambiguationData":[OSD([sQuery(id+"F2.wireOp",EDGE,"E13.18.0")])],"isStart":true});
            var Q88;
            {var subQ0=sQuery(id+"F2.wireOp",EDGE,"E0");Q88=makeQuery(id+"F3.opExtrude","CAP_EDGE",EDGE,{"disambiguationData":[OSD([subQ0]),TDD([makeQuery(id+"F2.imprint","IMPRINT",EDGE,{"disambiguationData":[TD([[makeQuery(id+"F2.imprint","INTERSECT",VERTEX,{"derivedFrom":[subQ0,sQuery(id+"F2.wireOp",EDGE,"E13.17.2")]}),-1.0]])],"derivedFrom":subQ0})])],"isStart":true});}
            var Q89;
            Q89=makeQuery(id+"F3.opExtrude","CAP_EDGE",EDGE,{"disambiguationData":[OSD([sQuery(id+"F2.wireOp",EDGE,"E13.17.2")])],"isStart":true});
            var Q90;
            Q90=makeQuery(id+"F3.opExtrude","CAP_EDGE",EDGE,{"disambiguationData":[OSD([sQuery(id+"F2.wireOp",EDGE,"E13.17.0")])],"isStart":true});
            var Q91;
            {var subQ0=sQuery(id+"F2.wireOp",EDGE,"E0");Q91=makeQuery(id+"F3.opExtrude","CAP_EDGE",EDGE,{"disambiguationData":[OSD([subQ0]),TDD([makeQuery(id+"F2.imprint","IMPRINT",EDGE,{"disambiguationData":[TD([[makeQuery(id+"F2.imprint","INTERSECT",VERTEX,{"derivedFrom":[subQ0,sQuery(id+"F2.wireOp",EDGE,"E13.16.2")]}),-1.0]])],"derivedFrom":subQ0})])],"isStart":true});}
            var Q92;
            Q92=makeQuery(id+"F3.opExtrude","CAP_EDGE",EDGE,{"disambiguationData":[OSD([sQuery(id+"F2.wireOp",EDGE,"E13.16.2")])],"isStart":true});
            var Q93;
            Q93=makeQuery(id+"F3.opExtrude","CAP_EDGE",EDGE,{"disambiguationData":[OSD([sQuery(id+"F2.wireOp",EDGE,"E13.16.0")])],"isStart":true});
            var Q94;
            {var subQ0=sQuery(id+"F2.wireOp",EDGE,"E0");Q94=makeQuery(id+"F3.opExtrude","CAP_EDGE",EDGE,{"disambiguationData":[OSD([subQ0]),TDD([makeQuery(id+"F2.imprint","IMPRINT",EDGE,{"disambiguationData":[TD([[makeQuery(id+"F2.imprint","INTERSECT",VERTEX,{"derivedFrom":[subQ0,sQuery(id+"F2.wireOp",EDGE,"E13.15.2")]}),-1.0]])],"derivedFrom":subQ0})])],"isStart":true});}
            var Q95;
            Q95=makeQuery(id+"F3.opExtrude","CAP_EDGE",EDGE,{"disambiguationData":[OSD([sQuery(id+"F2.wireOp",EDGE,"E13.15.2")])],"isStart":true});
            var Q96;
            Q96=makeQuery(id+"F3.opExtrude","CAP_EDGE",EDGE,{"disambiguationData":[OSD([sQuery(id+"F2.wireOp",EDGE,"E13.15.0")])],"isStart":true});
            var Q97;
            {var subQ0=sQuery(id+"F2.wireOp",EDGE,"E0");Q97=makeQuery(id+"F3.opExtrude","CAP_EDGE",EDGE,{"disambiguationData":[OSD([subQ0]),TDD([makeQuery(id+"F2.imprint","IMPRINT",EDGE,{"disambiguationData":[TD([[makeQuery(id+"F2.imprint","INTERSECT",VERTEX,{"derivedFrom":[subQ0,sQuery(id+"F2.wireOp",EDGE,"E13.14.2")]}),-1.0]])],"derivedFrom":subQ0})])],"isStart":true});}
            var Q98;
            Q98=makeQuery(id+"F3.opExtrude","CAP_EDGE",EDGE,{"disambiguationData":[OSD([sQuery(id+"F2.wireOp",EDGE,"E13.14.2")])],"isStart":true});
            var Q99;
            Q99=makeQuery(id+"F3.opExtrude","CAP_EDGE",EDGE,{"disambiguationData":[OSD([sQuery(id+"F2.wireOp",EDGE,"E13.14.0")])],"isStart":true});
            var Q100;
            {var subQ0=sQuery(id+"F2.wireOp",EDGE,"E0");Q100=makeQuery(id+"F3.opExtrude","CAP_EDGE",EDGE,{"disambiguationData":[OSD([subQ0]),TDD([makeQuery(id+"F2.imprint","IMPRINT",EDGE,{"disambiguationData":[TD([[makeQuery(id+"F2.imprint","INTERSECT",VERTEX,{"derivedFrom":[subQ0,sQuery(id+"F2.wireOp",EDGE,"E13.13.2")]}),-1.0]])],"derivedFrom":subQ0})])],"isStart":true});}
            var Q101;
            Q101=makeQuery(id+"F3.opExtrude","CAP_EDGE",EDGE,{"disambiguationData":[OSD([sQuery(id+"F2.wireOp",EDGE,"E13.13.2")])],"isStart":true});
            var Q102;
            Q102=makeQuery(id+"F3.opExtrude","CAP_EDGE",EDGE,{"disambiguationData":[OSD([sQuery(id+"F2.wireOp",EDGE,"E13.13.0")])],"isStart":true});
            var Q103;
            {var subQ0=sQuery(id+"F2.wireOp",EDGE,"E0");Q103=makeQuery(id+"F3.opExtrude","CAP_EDGE",EDGE,{"disambiguationData":[OSD([subQ0]),TDD([makeQuery(id+"F2.imprint","IMPRINT",EDGE,{"disambiguationData":[TD([[makeQuery(id+"F2.imprint","INTERSECT",VERTEX,{"derivedFrom":[subQ0,sQuery(id+"F2.wireOp",EDGE,"E13.12.2")]}),-1.0]])],"derivedFrom":subQ0})])],"isStart":true});}
            var Q104;
            Q104=makeQuery(id+"F3.opExtrude","CAP_EDGE",EDGE,{"disambiguationData":[OSD([sQuery(id+"F2.wireOp",EDGE,"E13.12.2")])],"isStart":true});
            var Q105;
            Q105=makeQuery(id+"F3.opExtrude","CAP_EDGE",EDGE,{"disambiguationData":[OSD([sQuery(id+"F2.wireOp",EDGE,"E13.12.0")])],"isStart":true});
            var Q106;
            {var subQ0=sQuery(id+"F2.wireOp",EDGE,"E0");Q106=makeQuery(id+"F3.opExtrude","CAP_EDGE",EDGE,{"disambiguationData":[OSD([subQ0]),TDD([makeQuery(id+"F2.imprint","IMPRINT",EDGE,{"disambiguationData":[TD([[makeQuery(id+"F2.imprint","INTERSECT",VERTEX,{"derivedFrom":[subQ0,sQuery(id+"F2.wireOp",EDGE,"E13.11.2")]}),-1.0]])],"derivedFrom":subQ0})])],"isStart":true});}
            var Q107;
            Q107=makeQuery(id+"F3.opExtrude","CAP_EDGE",EDGE,{"disambiguationData":[OSD([sQuery(id+"F2.wireOp",EDGE,"E13.11.2")])],"isStart":true});
            var Q108;
            Q108=makeQuery(id+"F3.opExtrude","CAP_EDGE",EDGE,{"disambiguationData":[OSD([sQuery(id+"F2.wireOp",EDGE,"E13.11.0")])],"isStart":true});
            var Q109;
            {var subQ0=sQuery(id+"F2.wireOp",EDGE,"E0");Q109=makeQuery(id+"F3.opExtrude","CAP_EDGE",EDGE,{"disambiguationData":[OSD([subQ0]),TDD([makeQuery(id+"F2.imprint","IMPRINT",EDGE,{"disambiguationData":[TD([[makeQuery(id+"F2.imprint","INTERSECT",VERTEX,{"derivedFrom":[subQ0,sQuery(id+"F2.wireOp",EDGE,"E13.10.2")]}),-1.0]])],"derivedFrom":subQ0})])],"isStart":true});}
            var Q110;
            Q110=makeQuery(id+"F3.opExtrude","CAP_EDGE",EDGE,{"disambiguationData":[OSD([sQuery(id+"F2.wireOp",EDGE,"E13.10.2")])],"isStart":true});
            var Q111;
            Q111=makeQuery(id+"F3.opExtrude","CAP_EDGE",EDGE,{"disambiguationData":[OSD([sQuery(id+"F2.wireOp",EDGE,"E13.10.0")])],"isStart":true});
            var Q112;
            {var subQ0=sQuery(id+"F2.wireOp",EDGE,"E0");Q112=makeQuery(id+"F3.opExtrude","CAP_EDGE",EDGE,{"disambiguationData":[OSD([subQ0]),TDD([makeQuery(id+"F2.imprint","IMPRINT",EDGE,{"disambiguationData":[TD([[makeQuery(id+"F2.imprint","INTERSECT",VERTEX,{"derivedFrom":[subQ0,sQuery(id+"F2.wireOp",EDGE,"E13.9.2")]}),-1.0]])],"derivedFrom":subQ0})])],"isStart":true});}
            var Q113;
            Q113=makeQuery(id+"F3.opExtrude","CAP_EDGE",EDGE,{"disambiguationData":[OSD([sQuery(id+"F2.wireOp",EDGE,"E13.9.2")])],"isStart":true});
            var Q114;
            Q114=makeQuery(id+"F3.opExtrude","CAP_EDGE",EDGE,{"disambiguationData":[OSD([sQuery(id+"F2.wireOp",EDGE,"E13.9.0")])],"isStart":true});
            var Q115;
            {var subQ0=sQuery(id+"F2.wireOp",EDGE,"E0");Q115=makeQuery(id+"F3.opExtrude","CAP_EDGE",EDGE,{"disambiguationData":[OSD([subQ0]),TDD([makeQuery(id+"F2.imprint","IMPRINT",EDGE,{"disambiguationData":[TD([[makeQuery(id+"F2.imprint","INTERSECT",VERTEX,{"derivedFrom":[subQ0,sQuery(id+"F2.wireOp",EDGE,"E13.8.2")]}),-1.0]])],"derivedFrom":subQ0})])],"isStart":true});}
            var Q116;
            Q116=makeQuery(id+"F3.opExtrude","CAP_EDGE",EDGE,{"disambiguationData":[OSD([sQuery(id+"F2.wireOp",EDGE,"E13.8.2")])],"isStart":true});
            fillet(context, id + "F4", {"entities" : qUnion([Q0, Q1, Q2, Q3, Q4, Q5, Q6, Q7, Q8, Q9, Q10, Q11, Q12, Q13, Q14, Q15, Q16, Q17, Q18, Q19, Q20, Q21, Q22, Q23, Q24, Q25, Q26, Q27, Q28, Q29, Q30, Q31, Q32, Q33, Q34, Q35, Q36, Q37, Q38, Q39, Q40, Q41, Q42, Q43, Q44, Q45, Q46, Q47, Q48, Q49, Q50, Q51, Q52, Q53, Q54, Q55, Q56, Q57, Q58, Q59, Q60, Q61, Q62, Q63, Q64, Q65, Q66, Q67, Q68, Q69, Q70, Q71, Q72, Q73, Q74, Q75, Q76, Q77, Q78, Q79, Q80, Q81, Q82, Q83, Q84, Q85, Q86, Q87, Q88, Q89, Q90, Q91, Q92, Q93, Q94, Q95, Q96, Q97, Q98, Q99, Q100, Q101, Q102, Q103, Q104, Q105, Q106, Q107, Q108, Q109, Q110, Q111, Q112, Q113, Q114, Q115, Q116]), "radius" : (getVariable(context, 'TeethFillet')) * mm, "tangentPropagation" : true, "allowEdgeOverflow" : false});
        }
    });
